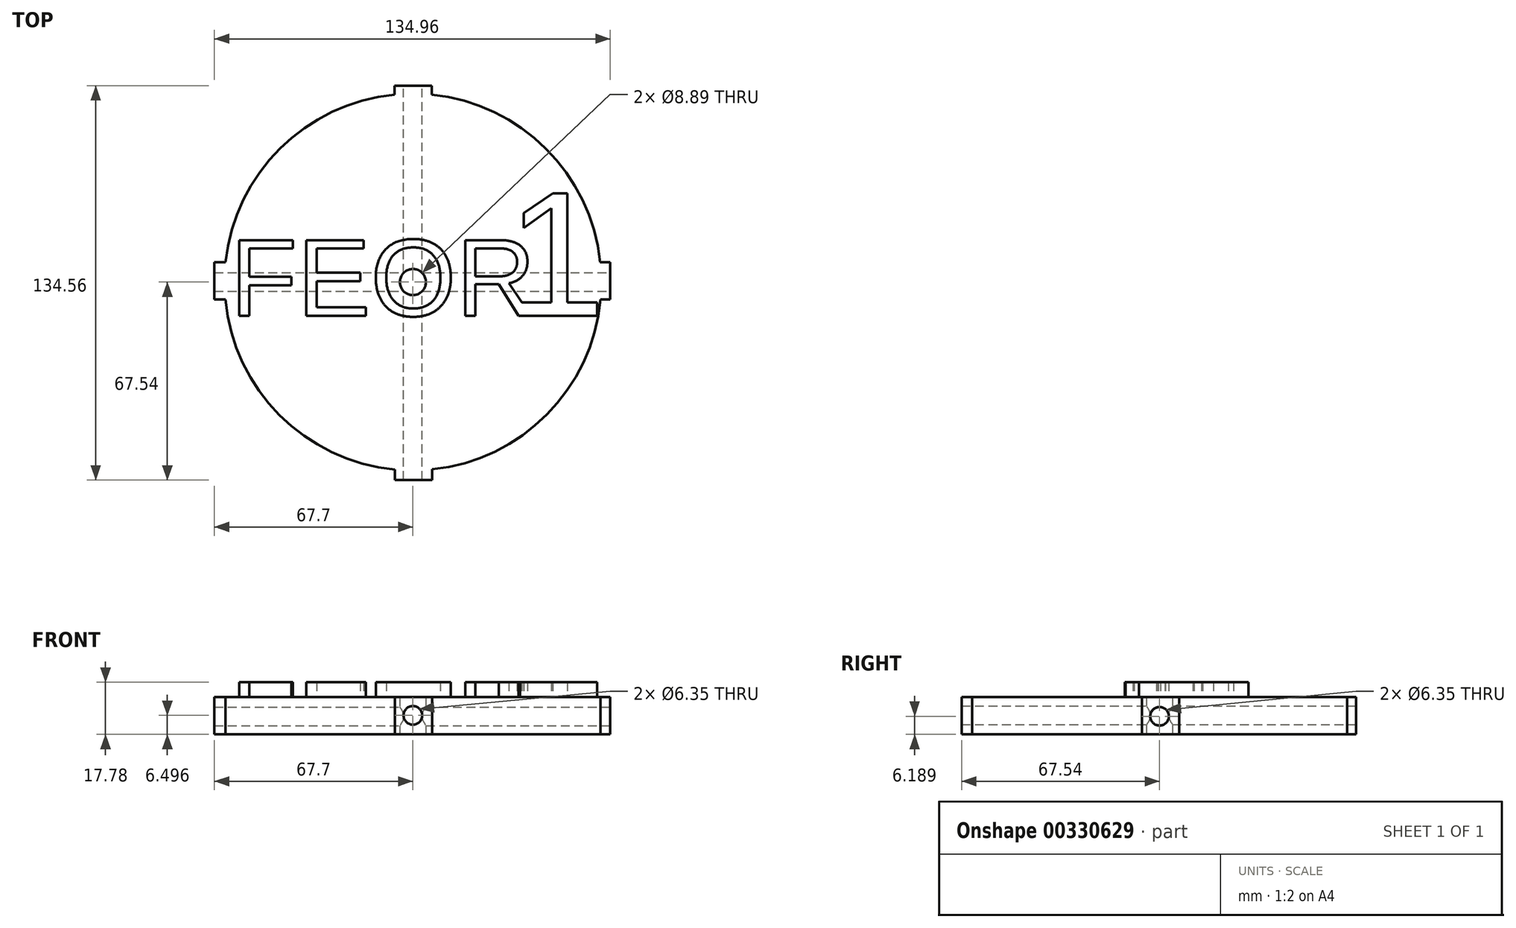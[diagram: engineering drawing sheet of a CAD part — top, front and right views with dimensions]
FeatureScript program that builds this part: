
annotation { "Feature Type Name" : "Feature", "Feature Type Description" : "" }
export const myFeature = defineFeature(function(context is Context, id is Id, definition is map)
    precondition{}
    {
        {
            var Q0;
            Q0=qCreatedBy(makeId("Top.planeOp"),FACE);
            var sketch = newSketch(context, id + "F0", { "sketchPlane" : qUnion([Q0])});
            skCircle(sketch, "E0", {"center": v(0, 0) * mm, "radius": 64.25 * mm});
            skSolve(sketch);
        }
        {
            var Q0;
            Q0=makeQuery(id+"F0.imprint","IMPRINT",FACE,{"disambiguationData":[TD([[makeQuery(id+"F0.imprint","IMPRINT",EDGE,{"derivedFrom":sQuery(id+"F0.wireOp",EDGE,"E0")}),1.0]])]});
            extrude(context, id + "F1", {"entities" : qUnion([Q0]), "depth" : 12.7 * mm});
        }
        {
            var Q0;
            Q0=makeQuery(id+"F1.opExtrude","CAP_FACE",FACE,{"disambiguationData":[OSD([sQuery(id+"F0.wireOp",EDGE,"E0")])],"isStart":false});
            var sketch = newSketch(context, id + "F2", { "sketchPlane" : qUnion([Q0])});
            skText(sketch, "E1", { "text": "FEOR", "fontName": "Arimo-Regular.ttf"});
            skText(sketch, "E2", { "text": "1", "fontName": "Arimo-Regular.ttf"});
            const initialGuessF2  = {"E1": [-0.06235, -0.0115, 1, 0, 0.027], "E2": [0.11425, -0.0106, 1, 0, 0.0542]};
            skSetInitialGuess(sketch, initialGuessF2);
            skSolve(sketch);
        }
        {
            var Q0;
            Q0=qCreatedBy(makeId("Top.planeOp"),FACE);
            var sketch = newSketch(context, id + "F3", { "sketchPlane" : qUnion([Q0])});
            skPoint(sketch, "E3", {"position": v(0, 0) * mm});
            skSolve(sketch);
        }
        {
            var Q0;
            Q0=sQuery(id+"F3.wireOp",VERTEX,"E3");
            var Q1;
            Q1=makeQuery(id+"F1.opExtrude","SWEPT_BODY",BODY,{"disambiguationData":[OSD([sQuery(id+"F0.wireOp",EDGE,"E0")])]});
            hole(context, id + "F4", {"style" : HoleStyle.SIMPLE, "endStyle" : HoleEndStyle.THROUGH, "oppositeDirection" : true, "holeDiameter" : 8.9 * mm, "tappedDepth" : 12.7 * mm, "tapClearance" : 3, "locations" : qUnion([Q0]), "scope" : qUnion([Q1])});
        }
        {
            var Q0;
            {var subQ9=sQuery(id+"F2.wireOp",EDGE,"E2.sketch_text.stroke-2");Q0=makeQuery(id+"F2.imprint","IMPRINT",FACE,{"disambiguationData":[TD([[makeQuery(id+"F2.imprint","IMPRINT",EDGE,{"derivedFrom":subQ9}),-1.0]])]});}
            var sketch = newSketch(context, id + "F5", { "sketchPlane" : qUnion([Q0])});
            skText(sketch, "E4", { "text": "1", "fontName": "Arimo-Regular.ttf"});
            const initialGuessF5  = {"E4": [0.03196, -0.01155, 1, 0, 0.04376]};
            skSetInitialGuess(sketch, initialGuessF5);
            skSolve(sketch);
        }
        {
            var Q0;
            Q0 = qSketchRegion(id + "F5", true);
            extrude(context, id + "F6", {"entities" : qUnion([Q0]), "operationType" : NewBodyOperationType.ADD, "depth" : 5.08 * mm});
        }
        {
            var Q0;
            Q0 = qSketchRegion(id + "F2", true);
            extrude(context, id + "F7", {"entities" : qUnion([Q0]), "operationType" : NewBodyOperationType.ADD, "depth" : 5.08 * mm});
        }
        {
            var Q0;
            Q0=makeQuery(id+"F7.opExtrude","SWEPT_FACE",FACE,{"disambiguationData":[OSD([sQuery(id+"F2.wireOp",EDGE,"E2.sketch_text.stroke-7")])]});
            extrude(context, id + "F8", {"entities" : qUnion([Q0]), "operationType" : NewBodyOperationType.REMOVE, "oppositeDirection" : true, "depth" : 25.4 * mm});
        }
        {
            var Q0;
            Q0=makeQuery(id+"F7.opExtrude","CAP_FACE",FACE,{"disambiguationData":[OSD([sQuery(id+"F2.wireOp",EDGE,"E2.sketch_text.stroke-0"),sQuery(id+"F2.wireOp",EDGE,"E2.sketch_text.stroke-1"),sQuery(id+"F2.wireOp",EDGE,"E2.sketch_text.stroke-2"),sQuery(id+"F2.wireOp",EDGE,"E2.sketch_text.stroke-3"),sQuery(id+"F2.wireOp",EDGE,"E2.sketch_text.stroke-4"),sQuery(id+"F2.wireOp",EDGE,"E2.sketch_text.stroke-5"),sQuery(id+"F2.wireOp",EDGE,"E2.sketch_text.stroke-6"),sQuery(id+"F2.wireOp",EDGE,"E2.sketch_text.stroke-7"),sQuery(id+"F2.wireOp",EDGE,"E2.sketch_text.stroke-8"),sQuery(id+"F2.wireOp",EDGE,"E2.sketch_text.stroke-9"),sQuery(id+"F2.wireOp",EDGE,"E2.sketch_text.stroke-10")])],"isStart":false});
            extrude(context, id + "F9", {"entities" : qUnion([Q0]), "operationType" : NewBodyOperationType.REMOVE, "oppositeDirection" : true, "depth" : 25.4 * mm});
        }
        {
            var Q0;
            Q0=qCreatedBy(makeId("Top.planeOp"),FACE);
            var sketch = newSketch(context, id + "F10", { "sketchPlane" : qUnion([Q0])});
            skLineSegment(sketch, "E5.bottom", {"start": v(-67.7, 6.71) * mm, "end": v(-60.45, 6.71) * mm});
            skLineSegment(sketch, "E5.top", {"start": v(-67.7, -5.99) * mm, "end": v(-60.45, -5.99) * mm});
            skLineSegment(sketch, "E5.left", {"start": v(-67.7, 6.71) * mm, "end": v(-67.7, -5.99) * mm});
            skLineSegment(sketch, "E5.right", {"start": v(-60.45, 6.71) * mm, "end": v(-60.45, -5.99) * mm});
            skLineSegment(sketch, "E6.bottom", {"start": v(-6.27, 67.02) * mm, "end": v(6.43, 67.02) * mm});
            skLineSegment(sketch, "E6.top", {"start": v(-6.27, 59.4) * mm, "end": v(6.43, 59.4) * mm});
            skLineSegment(sketch, "E6.left", {"start": v(-6.27, 67.02) * mm, "end": v(-6.27, 59.4) * mm});
            skLineSegment(sketch, "E6.right", {"start": v(6.43, 67.02) * mm, "end": v(6.43, 59.4) * mm});
            skLineSegment(sketch, "E7.bottom", {"start": v(59.64, 6.71) * mm, "end": v(67.26, 6.71) * mm});
            skLineSegment(sketch, "E7.top", {"start": v(59.64, -5.99) * mm, "end": v(67.26, -5.99) * mm});
            skLineSegment(sketch, "E7.left", {"start": v(59.64, 6.71) * mm, "end": v(59.64, -5.99) * mm});
            skLineSegment(sketch, "E7.right", {"start": v(67.26, 6.71) * mm, "end": v(67.26, -5.99) * mm});
            skLineSegment(sketch, "E8.bottom", {"start": v(-6.1, -59.92) * mm, "end": v(6.6, -59.92) * mm});
            skLineSegment(sketch, "E8.top", {"start": v(-6.1, -67.54) * mm, "end": v(6.6, -67.54) * mm});
            skLineSegment(sketch, "E8.left", {"start": v(-6.1, -59.92) * mm, "end": v(-6.1, -67.54) * mm});
            skLineSegment(sketch, "E8.right", {"start": v(6.6, -59.92) * mm, "end": v(6.6, -67.54) * mm});
            skSolve(sketch);
        }
        {
            var Q0;
            Q0=makeQuery(id+"F10.imprint","IMPRINT",FACE,{"disambiguationData":[TD([[makeQuery(id+"F10.imprint","IMPRINT",EDGE,{"derivedFrom":sQuery(id+"F10.wireOp",EDGE,"E5.bottom")}),-1.0]])]});
            var Q1;
            Q1=makeQuery(id+"F10.imprint","IMPRINT",FACE,{"disambiguationData":[TD([[makeQuery(id+"F10.imprint","IMPRINT",EDGE,{"derivedFrom":sQuery(id+"F10.wireOp",EDGE,"E6.bottom")}),-1.0]])]});
            var Q2;
            Q2=makeQuery(id+"F10.imprint","IMPRINT",FACE,{"disambiguationData":[TD([[makeQuery(id+"F10.imprint","IMPRINT",EDGE,{"derivedFrom":sQuery(id+"F10.wireOp",EDGE,"E7.bottom")}),-1.0]])]});
            var Q3;
            Q3=makeQuery(id+"F10.imprint","IMPRINT",FACE,{"disambiguationData":[TD([[makeQuery(id+"F10.imprint","IMPRINT",EDGE,{"derivedFrom":sQuery(id+"F10.wireOp",EDGE,"E8.bottom")}),-1.0]])]});
            extrude(context, id + "F11", {"entities" : qUnion([Q0, Q1, Q2, Q3]), "operationType" : NewBodyOperationType.ADD, "depth" : 12.7 * mm});
        }
        {
            var Q0;
            Q0=makeQuery(id+"F11.opExtrude","SWEPT_FACE",FACE,{"disambiguationData":[OSD([sQuery(id+"F10.wireOp",EDGE,"E7.right")])]});
            var sketch = newSketch(context, id + "F12", { "sketchPlane" : qUnion([Q0])});
            skPoint(sketch, "E9", {"position": v(0, 6.19) * mm});
            skPoint(sketch, "E10", {"position": v(52.73, -140.19) * mm});
            skSolve(sketch);
        }
        {
            var Q0;
            Q0=sQuery(id+"F12.wireOp",VERTEX,"E9");
            var Q1;
            Q1=makeQuery(id+"F1.opExtrude","SWEPT_BODY",BODY,{"disambiguationData":[OSD([sQuery(id+"F0.wireOp",EDGE,"E0")])]});
            hole(context, id + "F13", {"style" : HoleStyle.SIMPLE, "endStyle" : HoleEndStyle.THROUGH, "holeDiameter" : 6.35 * mm, "tappedDepth" : 12.7 * mm, "tapClearance" : 3, "locations" : qUnion([Q0]), "scope" : qUnion([Q1])});
        }
        {
            var Q0;
            Q0=makeQuery(id+"F11.opExtrude","SWEPT_FACE",FACE,{"disambiguationData":[OSD([sQuery(id+"F10.wireOp",EDGE,"E6.bottom")])]});
            var sketch = newSketch(context, id + "F14", { "sketchPlane" : qUnion([Q0])});
            skPoint(sketch, "E11", {"position": v(0, 6.5) * mm});
            skSolve(sketch);
        }
        {
            var Q0;
            Q0=sQuery(id+"F14.wireOp",VERTEX,"E11");
            var Q1;
            Q1=makeQuery(id+"F1.opExtrude","SWEPT_BODY",BODY,{"disambiguationData":[OSD([sQuery(id+"F0.wireOp",EDGE,"E0")])]});
            hole(context, id + "F15", {"style" : HoleStyle.SIMPLE, "endStyle" : HoleEndStyle.THROUGH, "holeDiameter" : 6.35 * mm, "tappedDepth" : 12.7 * mm, "tapClearance" : 3, "locations" : qUnion([Q0]), "scope" : qUnion([Q1])});
        }
    });
